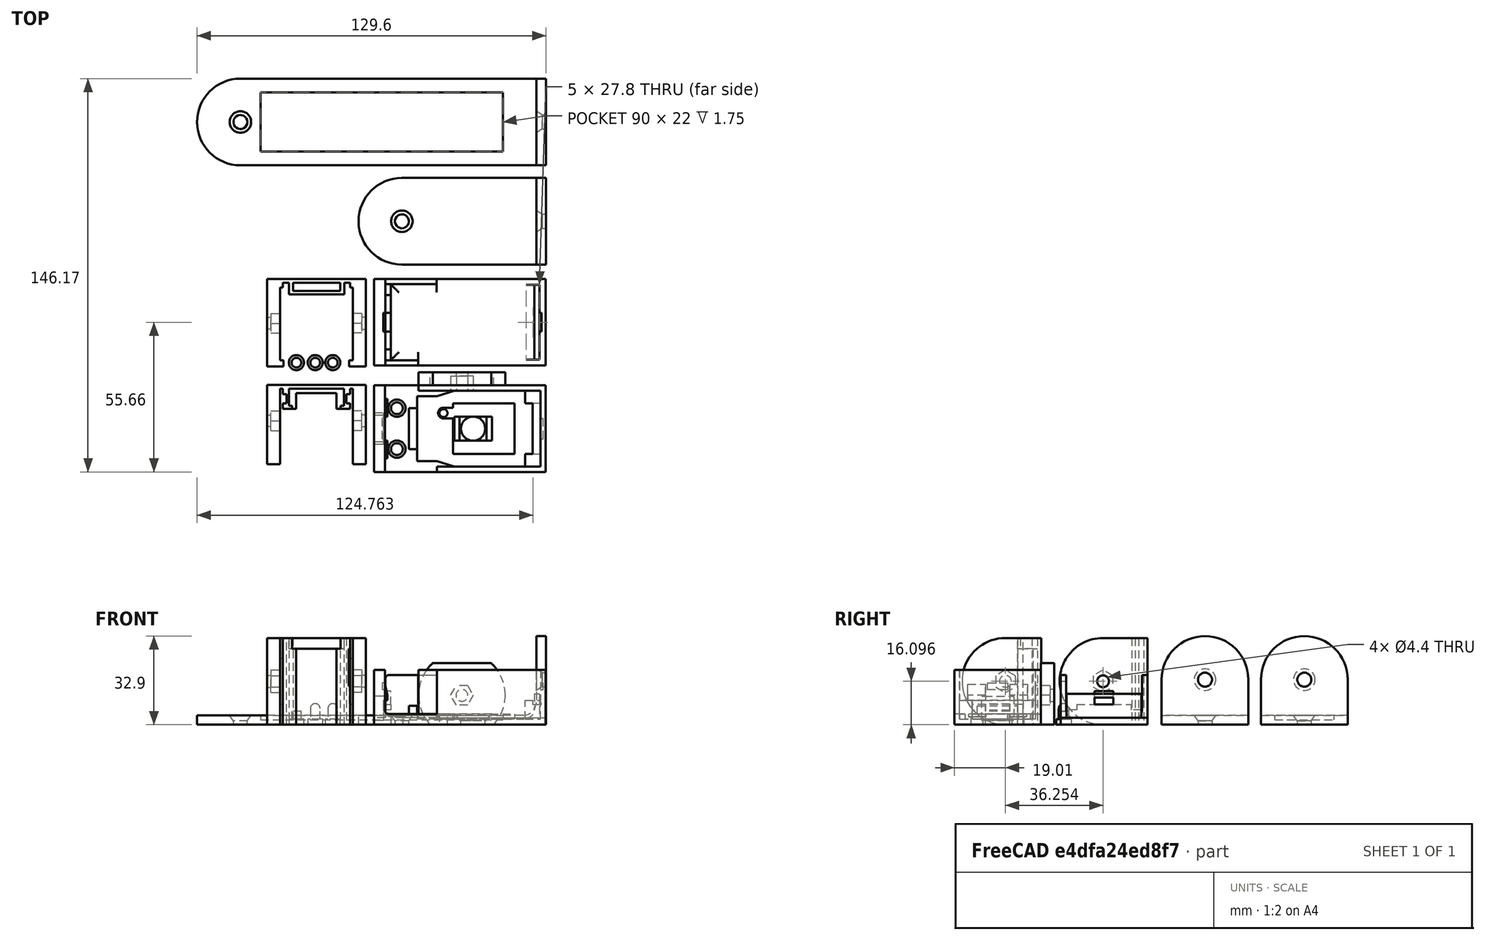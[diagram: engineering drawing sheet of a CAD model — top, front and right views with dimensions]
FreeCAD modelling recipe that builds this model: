
FCSTD DOCUMENT  (FreeCAD 0.18.4R)
Label: camera.wroover
License: All rights reserved
LicenseURL: http://en.wikipedia.org/wiki/All_rights_reserved
objects: Part::Part2DObjectPython×9, Part::MultiFuse×8, Part::Extrusion×8, Part::Feature×7, Part::Cut×4, Part::FeaturePython×4, App::DocumentObjectGroup×2
note: 40 computed .brp shape members not serialized (recipe doc carries the construction recipe); baked Part::Feature solids carry a one-line shape summary decoded from their .brp

FEATURE [Part::Feature] Cut051  label="Frame002"
  shape: bbox 63.8 x 37.1 x 22.84 mm, 112 faces (baked)
FEATURE [Part::Feature] Fusion005002002014004003003002009002010004002003006003008008004007002004008002005003003004019008  label="Cover001"
  shape: bbox 63.8 x 32.2 x 18.5 mm, 44 faces (baked)
FEATURE [Part::MultiFuse] Fusion005002002014004003003002009002010004002003006003008008004007002004008002005003003004009  label="Console"
  Placement = pos=(66.1287,37.5114,-1.47e-13) rot=(0,0,1;0rad)
FEATURE [Part::Feature] Fusion005002002014004003003002009002010004002003006003008008004007002004008002005003003004019003001  label="Rail-Reverse001"
  shape: bbox 36.79 x 32.6 x 32.2 mm, 42 faces (baked)
FEATURE [Part::MultiFuse] Fusion005002002014004003003002009002010004002003006003008008004007002004008002005003003004011  label="Rail-Straight"
FEATURE [Part::MultiFuse] Fusion005002002014004003003002009002010004002003006003008008004007002004008002003  label="Button 2"
  Placement = pos=(-38.6266,260.272,-1) rot=(0,0,1;0rad)
FEATURE [Part::MultiFuse] Fusion005002002014004003003002009002010004002003006003008008004007002004008002004  label="Button 1"
  Placement = pos=(-36.1997,260.259,-1) rot=(0,0,1;0rad)
FEATURE [Part::Feature] Slice_child0001  label="Button-cut"
  shape: bbox 5.6 x 5.6 x 5 mm, 5 faces (baked)
FEATURE [Part::Part2DObjectPython] Circle  # Draft 2D object (typed FeaturePython)
  FirstAngle = 0
  LastAngle = 0
  MakeFace = true
  Placement = pos=(-298.317,328.968,-7.13395) rot=(1,0,0;3.14159rad)
  Radius = 1.5
  Support = -> [Cut051]
FEATURE [Part::Extrusion] Extrusion
  Base = -> Circle
  Dir = (1.1e-14,-5.35e-14,28.9301)
  DirMode = 0
  FaceMakerClass = Part::FaceMakerBullseye
  LengthFwd = 0
  LengthRev = 0
  Solid = true
  Symmetric = false
FEATURE [Part::Cut] Cut  label="Frame"
  Base = -> Cut051
  Tool = -> Extrusion
FEATURE [Part::Part2DObjectPython] Rectangle  # Draft 2D object (typed FeaturePython)
  ChamferSize = 0
  Columns = 1
  FilletRadius = 0
  Height = 2.3
  Length = 2.3
  MakeFace = true
  Placement = pos=(-319.911,346.63,9.06605) rot=(1,0,0;1.5708rad)
  Rows = 1
FEATURE [Part::Extrusion] Extrusion001
  Base = -> Rectangle
  Dir = (-1.5e-15,2,-5.3e-15)
  DirMode = 0
  FaceMakerClass = Part::FaceMakerBullseye
  LengthFwd = 0
  LengthRev = 0
  Solid = true
  Symmetric = false
FEATURE [Part::MultiFuse] Fusion
  Shapes = -> [Fusion005002002014004003003002009002010004002003006003008008004007002004008002005003003004019008,Extrusion001]
FEATURE [Part::Part2DObjectPython] Circle002  # Draft 2D object (typed FeaturePython)
  FirstAngle = 0
  LastAngle = 0
  MakeFace = true
  Placement = pos=(-318.411,346.63,9.86605) rot=(1,0,0;1.5708rad)
  Radius = 1.5
  Support = -> [Fusion]
FEATURE [Part::Extrusion] Extrusion002
  Base = -> Circle002
  Dir = (-6.9e-15,9.3,-2.48e-14)
  DirMode = 0
  FaceMakerClass = Part::FaceMakerBullseye
  LengthFwd = 0
  LengthRev = 0
  Solid = true
  Symmetric = false
FEATURE [Part::Part2DObjectPython] Circle003  # Draft 2D object (typed FeaturePython)
  FirstAngle = 0
  LastAngle = 0
  MakeFace = true
  Placement = pos=(-318.411,346.63,9.86605) rot=(1,0,0;1.5708rad)
  Radius = 3.50777
  Support = -> [Fusion]
FEATURE [Part::Extrusion] Extrusion003
  Base = -> Circle003
  Dir = (-7.2e-15,9.3,-2.48e-14)
  DirMode = 0
  FaceMakerClass = Part::FaceMakerBullseye
  LengthFwd = 0
  LengthRev = 0
  Solid = true
  Symmetric = false
FEATURE [Part::Cut] Cut052
  Base = -> Extrusion003
  Tool = -> Extrusion002
FEATURE [Part::Part2DObjectPython] Rectangle001  # Draft 2D object (typed FeaturePython)
  ChamferSize = 0
  Columns = 1
  FilletRadius = 0
  Height = 15.0394
  Length = 32.2
  MakeFace = true
  Placement = pos=(-318.411,330.53,2.34633) rot=(0.57735,0.57735,0.57735;2.0944rad)
  Rows = 1
  Support = -> [Cut]
FEATURE [Part::FeaturePython] Slice  # WARN: FeaturePython — macro-defined, semantics opaque (R4)
  Base = -> Cut052
  Mode = 1
  Tolerance = 0
  Tools = -> [Rectangle001]
FEATURE [Part::FeaturePython] Slice_child1  label="Slice.1"  # WARN: FeaturePython — macro-defined, semantics opaque (R4)
  Base = -> Slice
  FilterType = 1
  Invert = false
  OverrideMaxVal = 0
  WindowFrom = 80
  WindowTo = 100
  items = 1
FEATURE [App::DocumentObjectGroup] GrExplode_Slice  label="Exploded Slice"
  Group = -> [Slice_child1]
FEATURE [Part::Part2DObjectPython] Rectangle002  # Draft 2D object (typed FeaturePython)
  ChamferSize = 0
  Columns = 1
  FilletRadius = 0
  Height = 39.5623
  Length = 16.9059
  MakeFace = true
  Placement = pos=(-309.958,366.411,9.86605) rot=(0,0,1;3.14159rad)
  Rows = 1
  Support = -> [Fusion]
FEATURE [Part::FeaturePython] Slice001  # WARN: FeaturePython — macro-defined, semantics opaque (R4)
  Base = -> Slice_child1
  Mode = 1
  Tolerance = 0
  Tools = -> [Rectangle002]
FEATURE [Part::FeaturePython] Slice001_child0  label="Slice001.0"  # WARN: FeaturePython — macro-defined, semantics opaque (R4)
  Base = -> Slice001
  FilterType = 1
  Invert = false
  OverrideMaxVal = 0
  WindowFrom = 80
  WindowTo = 100
  items = 0
FEATURE [Part::Part2DObjectPython] Rectangle003  # Draft 2D object (typed FeaturePython)
  ChamferSize = 0
  Columns = 1
  FilletRadius = 0
  Height = 9.15
  Length = 19
  MakeFace = true
  Placement = pos=(-319.911,378.83,11.3661) rot=(-1,0,0;1.5708rad)
  Rows = 1
FEATURE [Part::Extrusion] Extrusion004
  Base = -> Rectangle003
  Dir = (1.2e-15,-2,1.11e-14)
  DirMode = 0
  FaceMakerClass = Part::FaceMakerBullseye
  LengthFwd = 0
  LengthRev = 0
  Solid = true
  Symmetric = false
FEATURE [Part::MultiFuse] Fusion005002002014004003003002009002010004002003006003008008004007002004008002005003003004019003002
  Shapes = -> [Fusion,Extrusion004]
FEATURE [Part::Feature] Face001
  shape: bbox 3.508 x 3e-07 x 3.508 mm, 1 faces, 0 solids (baked)
FEATURE [Part::Extrusion] Extrusion005
  Base = -> Face001
  Dir = (-2.01e-14,26.0826,-6.95e-14)
  DirMode = 0
  FaceMakerClass = Part::FaceMakerBullseye
  LengthFwd = 0
  LengthRev = 0
  Solid = true
  Symmetric = false
FEATURE [Part::Cut] Cut053
  Base = -> Fusion005002002014004003003002009002010004002003006003008008004007002004008002005003003004019003002
  Tool = -> Extrusion005
FEATURE [Part::Cut] Cut054
  Base = -> Cut053
  Tool = -> Slice001_child0
FEATURE [App::DocumentObjectGroup] GrExplode_Slice001  label="Exploded Slice001"
  Group = -> [Cut054]
FEATURE [Part::Feature] Cut054001  label="Frame003"
  shape: bbox 63.8 x 32.2 x 18.5 mm, 45 faces (baked)
FEATURE [Part::Part2DObjectPython] Wire  # Draft 2D object (typed FeaturePython)
  ChamferSize = 0
  Closed = true
  End = (-261.873,359.23,0.366052)
  FilletRadius = 0
  Length = 5.85245
  MakeFace = true
  Placement = pos=(-262.617,359.23,2.86605) rot=(1,0,0;1.5708rad)
  Points = (3) [(0,0,0),(0,-2.5,0),(0.744074,-2.5,0)]
  Start = (-262.617,359.23,2.86605)
  Subdivisions = 0
FEATURE [Part::Extrusion] Extrusion006
  Base = -> Wire
  Dir = (2e-16,7,-1.6e-15)
  DirMode = 0
  FaceMakerClass = Part::FaceMakerBullseye
  LengthFwd = 0
  LengthRev = 0
  Solid = true
  Symmetric = false
FEATURE [Part::MultiFuse] Fusion005002002014004003003002009002010004002003006003008008004007002004008002005003003004019003003
  Shapes = -> [Extrusion006,Cut054001]
FEATURE [Part::Part2DObjectPython] Wire001  # Draft 2D object (typed FeaturePython)
  ChamferSize = 0
  Closed = true
  End = (-320.66,366.23,0.338701)
  FilletRadius = 0
  Length = 5.88614
  MakeFace = true
  Placement = pos=(-319.911,366.23,2.86605) rot=(-1,0,0;1.5708rad)
  Points = (3) [(0,0,0),(0,2.5,0),(-0.749501,2.52735,0)]
  Start = (-319.911,366.23,2.86605)
  Subdivisions = 0
FEATURE [Part::Extrusion] Extrusion007
  Base = -> Wire001
  Dir = (-2e-16,-7,-1.6e-15)
  DirMode = 0
  FaceMakerClass = Part::FaceMakerBullseye
  LengthFwd = 0
  LengthRev = 0
  Solid = true
  Symmetric = false
FEATURE [Part::MultiFuse] Fusion005002002014004003003002009002010004002003006003008008004007002004008002005003003004019003004
  Shapes = -> [Extrusion007,Fusion005002002014004003003002009002010004002003006003008008004007002004008002005003003004019003003]
FEATURE [Part::Feature] Cut001
  Placement = pos=(0,36.9,-2.576e-13) rot=(0,0,1;0rad)
  shape: bbox 129.6 x 32.2 x 32.9 mm, 18 faces (baked)
